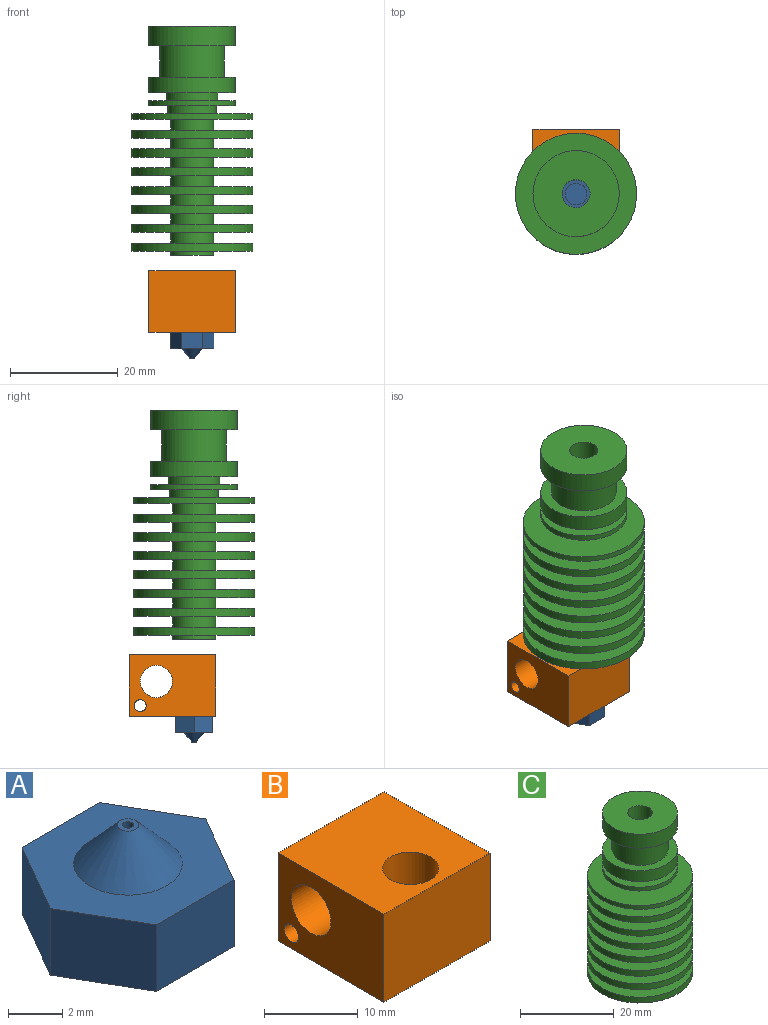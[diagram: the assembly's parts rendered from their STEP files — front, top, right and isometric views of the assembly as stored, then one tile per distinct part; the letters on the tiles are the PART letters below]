
ASSEMBLY  parts=3 mates=2
PART A: 14 faces, bbox 8.1x7x4.8 mm
  f0: plane 3.5x3mm, normal (0.87,-0.5,0), area 12.1mm2, adj f1,f5,f6,f7
  f1: plane 3.5x3mm, normal (0.87,0.5,0), area 12.1mm2, adj f0,f2,f6,f7
  f2: plane 4.04x3mm, normal (0,1,0), area 12.1mm2, adj f1,f3,f6,f7
  f3: plane 3.5x3mm, normal (-0.87,0.5,0), area 12.1mm2, adj f2,f4,f6,f7
  f4: plane 3.5x3mm, normal (-0.87,-0.5,0), area 12.1mm2, adj f3,f5,f6,f7
  f5: plane 4.04x3mm, normal (0,-1,0), area 12.1mm2, adj f0,f4,f6,f7
  f6: plane 8.08x7mm, normal (0,0,1), area 29.9mm2, adj f0,f1,f2,f3,f4,f5,f10
  f7: plane 8.08x7mm, normal (0,0,-1), area 29.9mm2, adj f0,f1,f2,f3,f4,f5,f12
  f8: cylinder r=0.2mm len=1.75mm, axis (0,0,-1), area 2.2mm2, adj f9,f11
  f9: plane 0.8x0.8mm, normal (0,0,1), area 0.4mm2, adj f8,f10
  f10: cone r=0.4mm half-angle=42.4deg, axis (0,0,-1), area 17.9mm2, adj f6,f9
  f11: plane 0.4x0.4mm, normal (0,0,1), area 0.1mm2, adj f8
  f12: cylinder r=2mm len=4mm, axis (0,0,-1), area 25.1mm2, adj f7,f13
  f13: plane 4x4mm, normal (0,0,-1), area 12.6mm2, adj f12
PART B: 9 faces, bbox 16x16x11.5 mm
  f0: plane 16x11.5mm, normal (0,-1,0), area 184mm2, adj f1,f3,f4,f5
  f1: plane 16x11.5mm, normal (1,0,0), area 151.9mm2, adj f0,f2,f4,f5,f7,f8
  f2: plane 16x11.5mm, normal (0,1,0), area 184mm2, adj f1,f3,f4,f5
  f3: plane 16x11.5mm, normal (-1,0,0), area 151.9mm2, adj f0,f2,f4,f5,f7,f8
  f4: plane 16x16mm, normal (0,0,1), area 227.7mm2, adj f0,f1,f2,f3,f6
  f5: plane 16x16mm, normal (0,0,-1), area 227.7mm2, adj f0,f1,f2,f3,f6
  f6: cylinder r=3mm len=11.5mm, axis (0,0,1), area 216.8mm2, adj f4,f5
  f7: cylinder r=1.1mm len=16mm, axis (1,0,0), area 110.6mm2, adj f1,f3
  f8: cylinder r=3mm len=16mm, axis (1,0,0), area 301.6mm2, adj f1,f3
PART C: 46 faces, bbox 22.5x22.5x42.6 mm
  f0: cylinder r=11.25mm len=22.5mm, axis (0,0,-1), area 70.7mm2, adj f4,f19
  f1: plane 8x8mm, normal (0,0,-1), area 29mm2, adj f3,f17
  f2: cylinder r=11.25mm len=22.5mm, axis (0,0,-1), area 106mm2, adj f18,f23
  f3: cylinder r=2.6mm len=42.62mm, axis (0,0,-1), area 696.3mm2, adj f1,f16
  f4: plane 22.5x22.5mm, normal (0,0,1), area 334.6mm2, adj f0,f5
  f5: cylinder r=4.48mm len=8.96mm, axis (0,0,-1), area 41.9mm2, adj f4,f6
  f6: plane 16x16mm, normal (0,0,-1), area 138mm2, adj f5,f7
  f7: cylinder r=8mm len=16mm, axis (0,0,-1), area 50.3mm2, adj f6,f8
  f8: plane 16x16mm, normal (0,0,1), area 128.7mm2, adj f7,f9
  f9: cylinder r=4.8mm len=9.6mm, axis (0,0,-1), area 43.4mm2, adj f8,f10
  f10: plane 16x16mm, normal (0,0,-1), area 128.7mm2, adj f9,f11
  f11: cylinder r=8mm len=16mm, axis (0,0,-1), area 143.8mm2, adj f10,f12
  f12: plane 16x16mm, normal (0,0,1), area 88mm2, adj f11,f13
  f13: cylinder r=6mm len=12mm, axis (0,0,-1), area 222.4mm2, adj f12,f14
  f14: plane 16x16mm, normal (0,0,-1), area 88mm2, adj f13,f15
  f15: cylinder r=8mm len=16mm, axis (0,0,-1), area 183.5mm2, adj f14,f16
  f16: plane 16x16mm, normal (0,0,1), area 179.8mm2, adj f3,f15
  f17: cylinder r=4mm len=8mm, axis (0,0,1), area 19.6mm2, adj f1,f18
  f18: plane 22.5x22.5mm, normal (0,0,-1), area 347.3mm2, adj f2,f17
  f19: plane 22.5x22.5mm, normal (0,0,-1), area 347.3mm2, adj f0,f21
  f20: plane 22.5x22.5mm, normal (0,0,1), area 347.3mm2, adj f21,f25
  f21: cylinder r=4mm len=8mm, axis (0,0,1), area 50.3mm2, adj f19,f20
  f22: plane 22.5x22.5mm, normal (0,0,-1), area 347.3mm2, adj f24,f29
  f23: plane 22.5x22.5mm, normal (0,0,1), area 347.3mm2, adj f2,f24
  f24: cylinder r=4mm len=8mm, axis (0,0,1), area 50.3mm2, adj f22,f23
  f25: cylinder r=11.25mm len=22.5mm, axis (0,0,-1), area 106mm2, adj f20,f26
  f26: plane 22.5x22.5mm, normal (0,0,-1), area 347.3mm2, adj f25,f28
  f27: plane 22.5x22.5mm, normal (0,0,1), area 347.3mm2, adj f28,f33
  f28: cylinder r=4mm len=8mm, axis (0,0,1), area 50.3mm2, adj f26,f27
  f29: cylinder r=11.25mm len=22.5mm, axis (0,0,-1), area 106mm2, adj f22,f31
  f30: plane 22.5x22.5mm, normal (0,0,-1), area 347.3mm2, adj f32,f37
  f31: plane 22.5x22.5mm, normal (0,0,1), area 347.3mm2, adj f29,f32
  f32: cylinder r=4mm len=8mm, axis (0,0,1), area 50.3mm2, adj f30,f31
  f33: cylinder r=11.25mm len=22.5mm, axis (0,0,-1), area 106mm2, adj f27,f34
  f34: plane 22.5x22.5mm, normal (0,0,-1), area 347.3mm2, adj f33,f36
  f35: plane 22.5x22.5mm, normal (0,0,1), area 347.3mm2, adj f36,f41
  f36: cylinder r=4mm len=8mm, axis (0,0,1), area 50.3mm2, adj f34,f35
  f37: cylinder r=11.25mm len=22.5mm, axis (0,0,-1), area 106mm2, adj f30,f39
  f38: plane 22.5x22.5mm, normal (0,0,-1), area 347.3mm2, adj f40,f42
  f39: plane 22.5x22.5mm, normal (0,0,1), area 347.3mm2, adj f37,f40
  f40: cylinder r=4mm len=8mm, axis (0,0,1), area 50.3mm2, adj f38,f39
  f41: cylinder r=11.25mm len=22.5mm, axis (0,0,-1), area 106mm2, adj f35,f43
  f42: cylinder r=11.25mm len=22.5mm, axis (0,0,-1), area 106mm2, adj f38,f44
  f43: plane 22.5x22.5mm, normal (0,0,-1), area 347.3mm2, adj f41,f45
  f44: plane 22.5x22.5mm, normal (0,0,1), area 347.3mm2, adj f42,f45
  f45: cylinder r=4mm len=8mm, axis (0,0,1), area 50.3mm2, adj f43,f44
PLACE A rot(axis=(1,0,0),180deg) t=(-2.75,3.27,-32.61)mm
PLACE B t=(-2.75,7.27,-32.61)mm
PLACE C t=(-2.75,3.27,-18.31)mm
MATE fastened A.f12 <-> B.f6  axis (0,0,1) through (-2.75,3.27,-32.61)mm
MATE fastened B.f6 <-> C.f0  axis (0,0,1) through (-2.75,3.27,-21.11)mm
